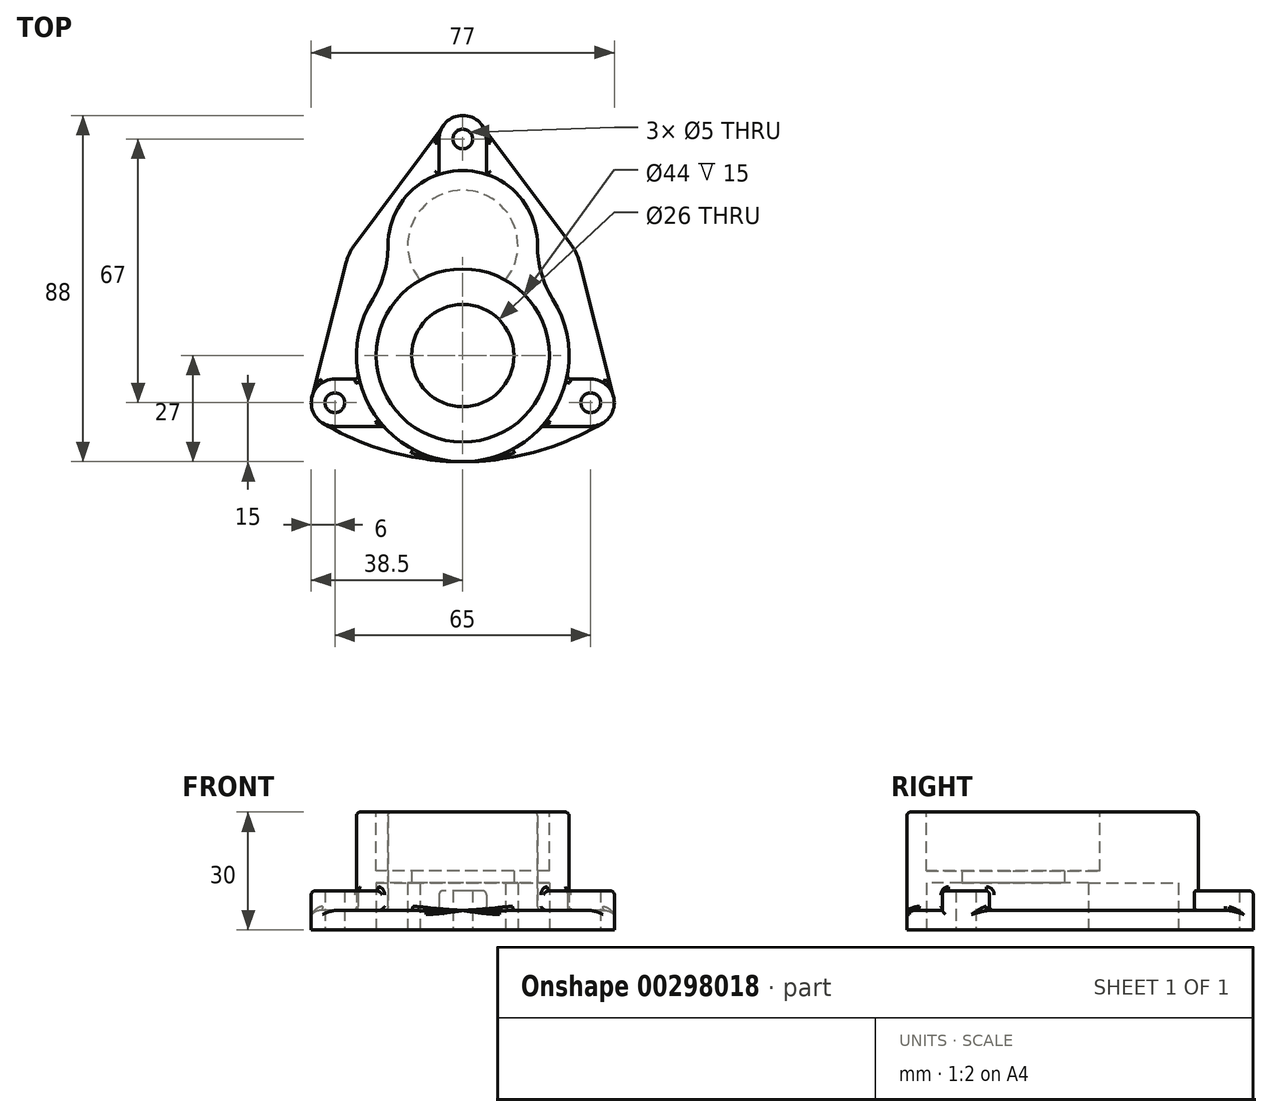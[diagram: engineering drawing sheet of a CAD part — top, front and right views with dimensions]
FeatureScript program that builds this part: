
annotation { "Feature Type Name" : "Feature", "Feature Type Description" : "" }
export const myFeature = defineFeature(function(context is Context, id is Id, definition is map)
    precondition{}
    {
        {
            var Q0;
            Q0=qCreatedBy(makeId("Top.planeOp"),FACE);
            var sketch = newSketch(context, id + "F0", { "sketchPlane" : qUnion([Q0])});
            skCircle(sketch, "E0", {"center": v(0, 0) * mm, "radius": 13 * mm});
            skCircle(sketch, "E1", {"center": v(0, 0) * mm, "radius": 22 * mm});
            skCircle(sketch, "E2", {"center": v(0, 0) * mm, "radius": 27 * mm});
            skCircle(sketch, "E3", {"center": v(32.5, -12) * mm, "radius": 6 * mm});
            skCircle(sketch, "E4", {"center": v(-32.5, -12) * mm, "radius": 6 * mm});
            skCircle(sketch, "E5", {"center": v(-32.5, -12) * mm, "radius": 2.5 * mm});
            skCircle(sketch, "E6", {"center": v(32.5, -12) * mm, "radius": 2.5 * mm});
            skCircle(sketch, "E7", {"center": v(0, 28) * mm, "radius": 14 * mm});
            skArc(sketch, "E8", {"start": v(17.49, 20.57) * mm, "mid": v(0, 47) * mm, "end": v(-17.49, 20.57) * mm});
            skCircle(sketch, "E9", {"center": v(0, 55) * mm, "radius": 6 * mm});
            skCircle(sketch, "E10", {"center": v(0, 55) * mm, "radius": 2.5 * mm});
            skLineSegment(sketch, "E11", {"start": v(-32.5, -18) * mm, "end": v(-20.12, -18) * mm});
            skLineSegment(sketch, "E12", {"start": v(32.5, -18) * mm, "end": v(20.12, -18) * mm});
            skLineSegment(sketch, "E13", {"start": v(32.5, -6) * mm, "end": v(26.32, -6) * mm});
            skLineSegment(sketch, "E14", {"start": v(-32.5, -6) * mm, "end": v(-26.32, -6) * mm});
            skPoint(sketch, "E15.endSnap0", {"position": v(0, 47) * mm});
            skLineSegment(sketch, "E16", {"start": v(6, 55) * mm, "end": v(6, 46.03) * mm});
            skLineSegment(sketch, "E17", {"start": v(-6, 55) * mm, "end": v(-6, 46.03) * mm});
            skArc(sketch, "E18", {"start": v(-27.52, 28.03) * mm, "mid": v(-28.77, 25.95) * mm, "end": v(-29.6, 23.66) * mm});
            skArc(sketch, "E19.trimOffspring", {"start": v(29.61, 23.79) * mm, "mid": v(28.78, 26.1) * mm, "end": v(27.51, 28.2) * mm});
            skLineSegment(sketch, "E20", {"start": v(-4.82, 58.58) * mm, "end": v(-27.52, 28.03) * mm});
            skLineSegment(sketch, "E21", {"start": v(4.8, 58.6) * mm, "end": v(27.51, 28.2) * mm});
            skLineSegment(sketch, "E22", {"start": v(-29.6, 23.66) * mm, "end": v(-38.31, -10.52) * mm});
            skLineSegment(sketch, "E23", {"start": v(29.61, 23.79) * mm, "end": v(38.32, -10.52) * mm});
            skArc(sketch, "E24", {"start": v(0, -27) * mm, "mid": v(18.46, -24.5) * mm, "end": v(35.59, -17.15) * mm});
            skArc(sketch, "E25", {"start": v(-35.59, -17.15) * mm, "mid": v(-18.46, -24.5) * mm, "end": v(0, -27) * mm});
            skPoint(sketch, "E26.orphan", {"position": v(35.59, -17.15) * mm});
            skSolve(sketch);
        }
        {
            var Q0;
            {var subQ0=sQuery(id+"F0.wireOp",EDGE,"E8");var subQ1=sQuery(id+"F0.wireOp",EDGE,"E2");var subQ2=makeQuery(id+"F0.imprint","INTERSECT",VERTEX,{"disambiguationData":[OD(0.0)],"derivedFrom":[subQ1,subQ0]});Q0=makeQuery(id+"F0.imprint","IMPRINT",FACE,{"disambiguationData":[TD([[makeQuery(id+"F0.imprint","IMPRINT",EDGE,{"disambiguationData":[TD([[subQ2,-1.0]])],"derivedFrom":subQ1}),-1.0]])]});}
            var Q1;
            {var subQ0=sQuery(id+"F0.wireOp",EDGE,"E7");var subQ1=sQuery(id+"F0.wireOp",EDGE,"E1");var subQ2=makeQuery(id+"F0.imprint","INTERSECT",VERTEX,{"disambiguationData":[OD(0.0)],"derivedFrom":[subQ1,subQ0]});Q1=makeQuery(id+"F0.imprint","IMPRINT",FACE,{"disambiguationData":[TD([[makeQuery(id+"F0.imprint","IMPRINT",EDGE,{"disambiguationData":[TD([[subQ2,-1.0]])],"derivedFrom":subQ1}),-1.0]])]});}
            var Q2;
            {var subQ0=sQuery(id+"F0.wireOp",EDGE,"E7");var subQ1=sQuery(id+"F0.wireOp",EDGE,"E1");var subQ2=makeQuery(id+"F0.imprint","INTERSECT",VERTEX,{"disambiguationData":[OD(0.0)],"derivedFrom":[subQ1,subQ0]});Q2=makeQuery(id+"F0.imprint","IMPRINT",FACE,{"disambiguationData":[TD([[makeQuery(id+"F0.imprint","IMPRINT",EDGE,{"disambiguationData":[TD([[subQ2,1.0]])],"derivedFrom":subQ1}),-1.0]])]});}
            var Q3;
            {var subQ0=sQuery(id+"F0.wireOp",EDGE,"E7");var subQ1=sQuery(id+"F0.wireOp",EDGE,"E1");var subQ2=makeQuery(id+"F0.imprint","INTERSECT",VERTEX,{"disambiguationData":[OD(0.0)],"derivedFrom":[subQ1,subQ0]});Q3=makeQuery(id+"F0.imprint","IMPRINT",FACE,{"disambiguationData":[TD([[makeQuery(id+"F0.imprint","IMPRINT",EDGE,{"disambiguationData":[TD([[subQ2,1.0]])],"derivedFrom":subQ1}),1.0]])]});}
            var Q4;
            Q4=makeQuery(id+"F0.imprint","IMPRINT",FACE,{"disambiguationData":[TD([[makeQuery(id+"F0.imprint","IMPRINT",EDGE,{"derivedFrom":sQuery(id+"F0.wireOp",EDGE,"E0")}),-1.0]])]});
            var Q5;
            {var subQ0=sQuery(id+"F0.wireOp",EDGE,"E7");var subQ1=sQuery(id+"F0.wireOp",EDGE,"E2");var subQ2=makeQuery(id+"F0.imprint","INTERSECT",VERTEX,{"disambiguationData":[OD(0.0)],"derivedFrom":[subQ1,subQ0]});Q5=makeQuery(id+"F0.imprint","IMPRINT",FACE,{"disambiguationData":[TD([[makeQuery(id+"F0.imprint","IMPRINT",EDGE,{"disambiguationData":[TD([[subQ2,-1.0]])],"derivedFrom":subQ1}),-1.0]])]});}
            var Q6;
            Q6=makeQuery(id+"F0.imprint","IMPRINT",FACE,{"disambiguationData":[TD([[makeQuery(id+"F0.imprint","IMPRINT",EDGE,{"derivedFrom":sQuery(id+"F0.wireOp",EDGE,"E0")}),1.0]])]});
            extrude(context, id + "F1", {"entities" : qUnion([Q0, Q1, Q2, Q3, Q4, Q5, Q6]), "depth" : 30 * mm});
        }
        {
            var Q0;
            {var subQ0=sQuery(id+"F0.wireOp",EDGE,"E8");var subQ1=sQuery(id+"F0.wireOp",EDGE,"E2");Q0=makeQuery(id+"F1.opExtrude","SWEPT_EDGE",EDGE,{"disambiguationData":[OSD([subQ1,subQ0]),TDD([makeQuery(id+"F0.imprint","INTERSECT",VERTEX,{"disambiguationData":[OD(1.0)],"derivedFrom":[subQ1,subQ0]})])]});}
            var Q1;
            {var subQ0=sQuery(id+"F0.wireOp",EDGE,"E8");var subQ1=sQuery(id+"F0.wireOp",EDGE,"E2");Q1=makeQuery(id+"F1.opExtrude","SWEPT_EDGE",EDGE,{"disambiguationData":[OSD([subQ1,subQ0]),TDD([makeQuery(id+"F0.imprint","INTERSECT",VERTEX,{"disambiguationData":[OD(0.0)],"derivedFrom":[subQ1,subQ0]})])]});}
            fillet(context, id + "F2", {"entities" : qUnion([Q0, Q1]), "radius" : 25 * mm, "tangentPropagation" : true, "allowEdgeOverflow" : false});
        }
        {
            var Q0;
            {var subQ0=sQuery(id+"F0.wireOp",EDGE,"E16");Q0=makeQuery(id+"F0.imprint","IMPRINT",FACE,{"disambiguationData":[TD([[makeQuery(id+"F0.imprint","IMPRINT",EDGE,{"derivedFrom":subQ0}),-1.0]])]});}
            var Q1;
            {var subQ0=sQuery(id+"F0.wireOp",EDGE,"E12");Q1=makeQuery(id+"F0.imprint","IMPRINT",FACE,{"disambiguationData":[TD([[makeQuery(id+"F0.imprint","IMPRINT",EDGE,{"derivedFrom":subQ0}),-1.0]])]});}
            var Q2;
            Q2=makeQuery(id+"F0.imprint","IMPRINT",FACE,{"disambiguationData":[TD([[makeQuery(id+"F0.imprint","IMPRINT",EDGE,{"derivedFrom":sQuery(id+"F0.wireOp",EDGE,"E6")}),-1.0]])]});
            var Q3;
            {var subQ0=sQuery(id+"F0.wireOp",EDGE,"E11");Q3=makeQuery(id+"F0.imprint","IMPRINT",FACE,{"disambiguationData":[TD([[makeQuery(id+"F0.imprint","IMPRINT",EDGE,{"derivedFrom":subQ0}),1.0]])]});}
            var Q4;
            Q4=makeQuery(id+"F0.imprint","IMPRINT",FACE,{"disambiguationData":[TD([[makeQuery(id+"F0.imprint","IMPRINT",EDGE,{"derivedFrom":sQuery(id+"F0.wireOp",EDGE,"E5")}),-1.0]])]});
            var Q5;
            Q5=makeQuery(id+"F0.imprint","IMPRINT",FACE,{"disambiguationData":[TD([[makeQuery(id+"F0.imprint","IMPRINT",EDGE,{"derivedFrom":sQuery(id+"F0.wireOp",EDGE,"E10")}),-1.0]])]});
            extrude(context, id + "F3", {"entities" : qUnion([Q0, Q1, Q2, Q3, Q4, Q5]), "operationType" : NewBodyOperationType.ADD, "depth" : 10 * mm});
        }
        {
            var Q0;
            {var subQ4=sQuery(id+"F0.wireOp",EDGE,"E14");Q0=makeQuery(id+"F0.imprint","IMPRINT",FACE,{"disambiguationData":[TD([[makeQuery(id+"F0.imprint","IMPRINT",EDGE,{"derivedFrom":subQ4}),1.0]])]});}
            var Q1;
            {var subQ3=sQuery(id+"F0.wireOp",EDGE,"E13");Q1=makeQuery(id+"F0.imprint","IMPRINT",FACE,{"disambiguationData":[TD([[makeQuery(id+"F0.imprint","IMPRINT",EDGE,{"derivedFrom":subQ3}),-1.0]])]});}
            var Q2;
            {var subQ0=sQuery(id+"F0.wireOp",EDGE,"E12");Q2=makeQuery(id+"F0.imprint","IMPRINT",FACE,{"disambiguationData":[TD([[makeQuery(id+"F0.imprint","IMPRINT",EDGE,{"derivedFrom":subQ0}),1.0]])]});}
            var Q3;
            {var subQ0=sQuery(id+"F0.wireOp",EDGE,"E11");Q3=makeQuery(id+"F0.imprint","IMPRINT",FACE,{"disambiguationData":[TD([[makeQuery(id+"F0.imprint","IMPRINT",EDGE,{"derivedFrom":subQ0}),-1.0]])]});}
            extrude(context, id + "F4", {"entities" : qUnion([Q0, Q1, Q2, Q3]), "operationType" : NewBodyOperationType.ADD, "depth" : 5 * mm});
        }
        {
            var Q0;
            {var subQ0=sQuery(id+"F0.wireOp",EDGE,"E7");var subQ1=sQuery(id+"F0.wireOp",EDGE,"E2");var subQ2=makeQuery(id+"F0.imprint","INTERSECT",VERTEX,{"disambiguationData":[OD(0.0)],"derivedFrom":[subQ1,subQ0]});Q0=makeQuery(id+"F0.imprint","IMPRINT",FACE,{"disambiguationData":[TD([[makeQuery(id+"F0.imprint","IMPRINT",EDGE,{"disambiguationData":[TD([[subQ2,-1.0]])],"derivedFrom":subQ1}),-1.0]])]});}
            var Q1;
            {var subQ0=sQuery(id+"F0.wireOp",EDGE,"E7");var subQ1=sQuery(id+"F0.wireOp",EDGE,"E1");var subQ2=makeQuery(id+"F0.imprint","INTERSECT",VERTEX,{"disambiguationData":[OD(0.0)],"derivedFrom":[subQ1,subQ0]});Q1=makeQuery(id+"F0.imprint","IMPRINT",FACE,{"disambiguationData":[TD([[makeQuery(id+"F0.imprint","IMPRINT",EDGE,{"disambiguationData":[TD([[subQ2,1.0]])],"derivedFrom":subQ1}),-1.0]])]});}
            var Q2;
            {var subQ0=sQuery(id+"F0.wireOp",EDGE,"E7");var subQ1=sQuery(id+"F0.wireOp",EDGE,"E1");var subQ2=makeQuery(id+"F0.imprint","INTERSECT",VERTEX,{"disambiguationData":[OD(0.0)],"derivedFrom":[subQ1,subQ0]});Q2=makeQuery(id+"F0.imprint","IMPRINT",FACE,{"disambiguationData":[TD([[makeQuery(id+"F0.imprint","IMPRINT",EDGE,{"disambiguationData":[TD([[subQ2,1.0]])],"derivedFrom":subQ1}),1.0]])]});}
            var Q3;
            Q3=makeQuery(id+"F0.imprint","IMPRINT",FACE,{"disambiguationData":[TD([[makeQuery(id+"F0.imprint","IMPRINT",EDGE,{"derivedFrom":sQuery(id+"F0.wireOp",EDGE,"E0")}),-1.0]])]});
            var Q4;
            Q4=makeQuery(id+"F0.imprint","IMPRINT",FACE,{"disambiguationData":[TD([[makeQuery(id+"F0.imprint","IMPRINT",EDGE,{"derivedFrom":sQuery(id+"F0.wireOp",EDGE,"E0")}),1.0]])]});
            extrude(context, id + "F5", {"entities" : qUnion([Q0, Q1, Q2, Q3, Q4]), "operationType" : NewBodyOperationType.REMOVE, "depth" : 12 * mm});
        }
        {
            var Q0;
            Q0=makeQuery(id+"F1.opExtrude","CAP_FACE",FACE,{"disambiguationData":[OSD([sQuery(id+"F0.wireOp",EDGE,"E2"),sQuery(id+"F0.wireOp",EDGE,"E8")])],"isStart":false});
            var sketch = newSketch(context, id + "F6", { "sketchPlane" : qUnion([Q0])});
            skCircle(sketch, "E27.0", {"center": v(0, 0) * mm, "radius": 22 * mm});
            skSolve(sketch);
        }
        {
            var Q0;
            Q0 = qSketchRegion(id + "F6", true);
            extrude(context, id + "F7", {"entities" : qUnion([Q0]), "operationType" : NewBodyOperationType.REMOVE, "oppositeDirection" : true, "depth" : 15 * mm});
        }
        {
            var Q0;
            Q0=makeQuery(id+"F0.imprint","IMPRINT",FACE,{"disambiguationData":[TD([[makeQuery(id+"F0.imprint","IMPRINT",EDGE,{"derivedFrom":sQuery(id+"F0.wireOp",EDGE,"E0")}),1.0]])]});
            extrude(context, id + "F8", {"entities" : qUnion([Q0]), "operationType" : NewBodyOperationType.REMOVE, "endBound" : BoundingType.THROUGH_ALL, "depth" : 25 * mm});
        }
        {
            var Q0;
            Q0=makeQuery(id+"F4.opExtrude","CAP_FACE",FACE,{"disambiguationData":[OSD([sQuery(id+"F0.wireOp",EDGE,"E2"),sQuery(id+"F0.wireOp",EDGE,"E3"),sQuery(id+"F0.wireOp",EDGE,"E8"),sQuery(id+"F0.wireOp",EDGE,"E9"),sQuery(id+"F0.wireOp",EDGE,"E13"),sQuery(id+"F0.wireOp",EDGE,"E16"),sQuery(id+"F0.wireOp",EDGE,"E19.trimOffspring"),sQuery(id+"F0.wireOp",EDGE,"E21"),sQuery(id+"F0.wireOp",EDGE,"E23")])],"isStart":false});
            var Q1;
            Q1=makeQuery(id+"F4.opExtrude","CAP_FACE",FACE,{"disambiguationData":[OSD([sQuery(id+"F0.wireOp",EDGE,"E2"),sQuery(id+"F0.wireOp",EDGE,"E4"),sQuery(id+"F0.wireOp",EDGE,"E8"),sQuery(id+"F0.wireOp",EDGE,"E9"),sQuery(id+"F0.wireOp",EDGE,"E14"),sQuery(id+"F0.wireOp",EDGE,"E17"),sQuery(id+"F0.wireOp",EDGE,"E18"),sQuery(id+"F0.wireOp",EDGE,"E20"),sQuery(id+"F0.wireOp",EDGE,"E22")])],"isStart":false});
            var Q2;
            Q2=makeQuery(id+"F3.opExtrude","CAP_EDGE",EDGE,{"disambiguationData":[OSD([sQuery(id+"F0.wireOp",EDGE,"E16")])],"isStart":false});
            var Q3;
            Q3=makeQuery(id+"F3.opExtrude","CAP_EDGE",EDGE,{"disambiguationData":[OSD([sQuery(id+"F0.wireOp",EDGE,"E12")])],"isStart":false});
            var Q4;
            Q4=makeQuery(id+"F3.opExtrude","CAP_EDGE",EDGE,{"disambiguationData":[OSD([sQuery(id+"F0.wireOp",EDGE,"E11")])],"isStart":false});
            var Q5;
            Q5=makeQuery(id+"F4.opExtrude","CAP_EDGE",EDGE,{"disambiguationData":[OSD([sQuery(id+"F0.wireOp",EDGE,"E12")])],"isStart":false});
            var Q6;
            Q6=makeQuery(id+"F4.opExtrude","CAP_EDGE",EDGE,{"disambiguationData":[OSD([sQuery(id+"F0.wireOp",EDGE,"E11")])],"isStart":false});
            var Q7;
            {var subQ0=sQuery(id+"F0.wireOp",EDGE,"E2");Q7=makeQuery(id+"F4.opExtrude","CAP_EDGE",EDGE,{"disambiguationData":[OSD([subQ0]),TDD([makeQuery(id+"F0.imprint","IMPRINT",EDGE,{"disambiguationData":[TD([[makeQuery(id+"F0.imprint","INTERSECT",VERTEX,{"derivedFrom":[subQ0,sQuery(id+"F0.wireOp",EDGE,"E11")]}),-1.0]])],"derivedFrom":subQ0})])],"isStart":false});}
            var Q8;
            {var subQ0=sQuery(id+"F0.wireOp",EDGE,"E2");Q8=makeQuery(id+"F4.opExtrude","CAP_EDGE",EDGE,{"disambiguationData":[OSD([subQ0]),TDD([makeQuery(id+"F0.imprint","IMPRINT",EDGE,{"disambiguationData":[TD([[makeQuery(id+"F0.imprint","INTERSECT",VERTEX,{"derivedFrom":[subQ0,sQuery(id+"F0.wireOp",EDGE,"E12")]}),1.0]])],"derivedFrom":subQ0})])],"isStart":false});}
            fillet(context, id + "F9", {"entities" : qUnion([Q0, Q1, Q2, Q3, Q4, Q5, Q6, Q7, Q8]), "radius" : 1 * mm, "tangentPropagation" : true, "allowEdgeOverflow" : false});
        }
        {
            var Q0;
            Q0=makeQuery(id+"F4.opExtrude","CAP_EDGE",EDGE,{"disambiguationData":[OSD([sQuery(id+"F0.wireOp",EDGE,"E25")])],"isStart":false});
            var Q1;
            Q1=makeQuery(id+"F4.opExtrude","CAP_EDGE",EDGE,{"disambiguationData":[OSD([sQuery(id+"F0.wireOp",EDGE,"E24")])],"isStart":false});
            fillet(context, id + "F10", {"entities" : qUnion([Q0, Q1]), "radius" : 1 * mm, "tangentPropagation" : true, "allowEdgeOverflow" : false});
        }
        {
            var Q0;
            Q0=makeQuery(id+"F1.opExtrude","SWEPT_FACE",FACE,{"disambiguationData":[OSD([sQuery(id+"F0.wireOp",EDGE,"E2")])]});
            fillet(context, id + "F11", {"entities" : qUnion([Q0]), "radius" : 1 * mm, "tangentPropagation" : true, "allowEdgeOverflow" : false});
        }
    });
